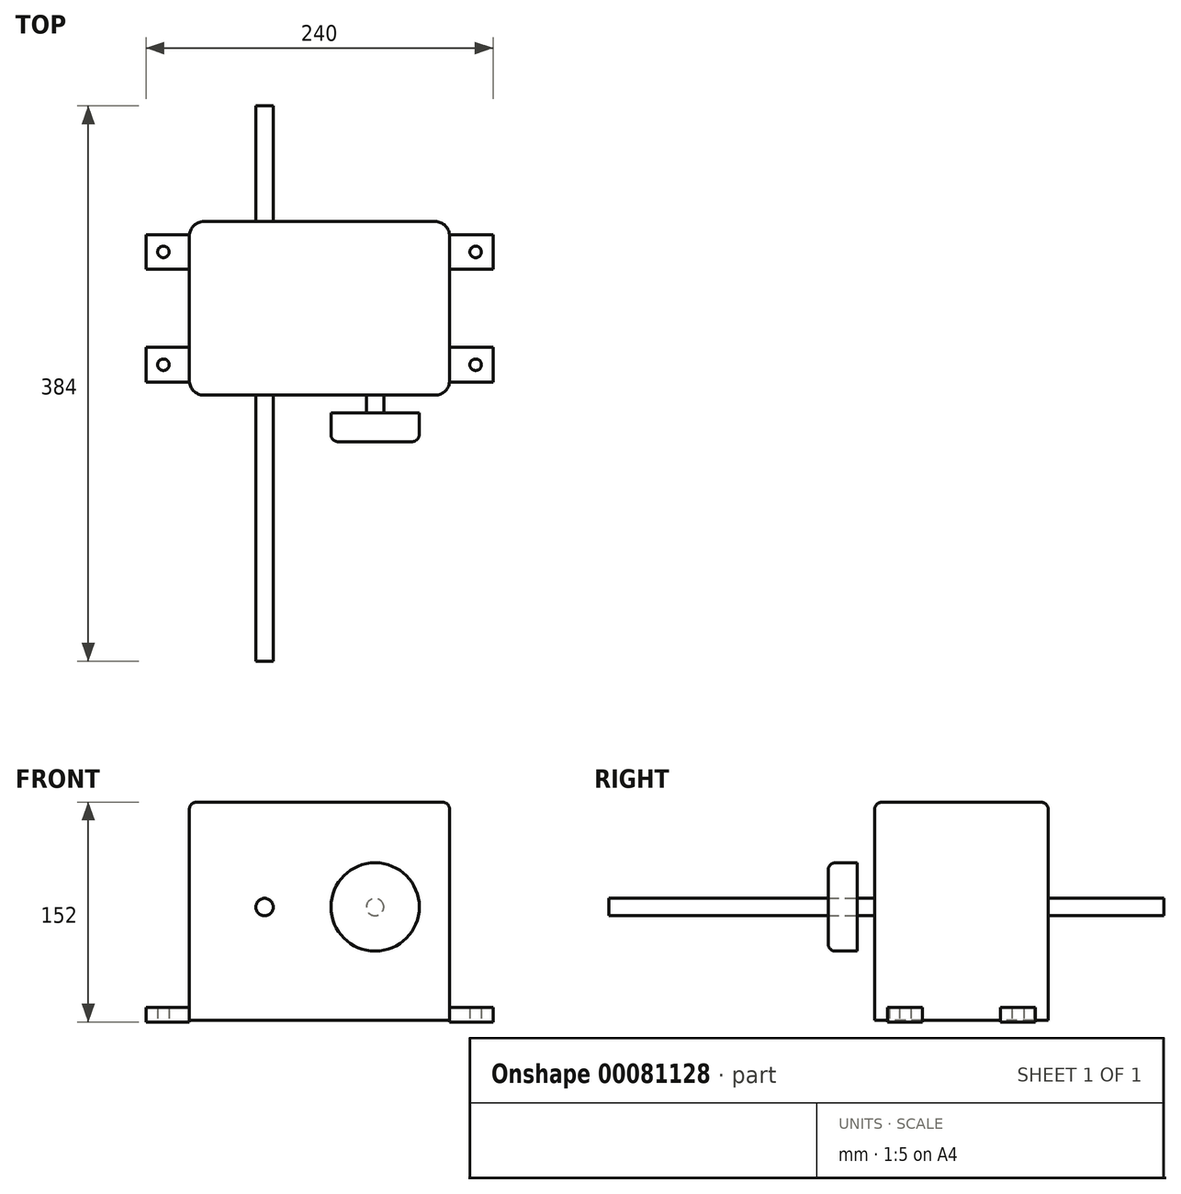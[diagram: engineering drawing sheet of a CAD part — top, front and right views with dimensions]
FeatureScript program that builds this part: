
annotation { "Feature Type Name" : "Feature", "Feature Type Description" : "" }
export const myFeature = defineFeature(function(context is Context, id is Id, definition is map)
    precondition{}
    {
        {
            var Q0;
            Q0=qCreatedBy(makeId("Top.planeOp"),FACE);
            var sketch = newSketch(context, id + "F0", { "sketchPlane" : qUnion([Q0])});
            skLineSegment(sketch, "E0.bottom", {"start": v(-90, 60) * mm, "end": v(90, 60) * mm});
            skLineSegment(sketch, "E0.top", {"start": v(-90, -60) * mm, "end": v(90, -60) * mm});
            skLineSegment(sketch, "E0.left", {"start": v(-90, 60) * mm, "end": v(-90, -60) * mm});
            skLineSegment(sketch, "E0.right", {"start": v(90, 60) * mm, "end": v(90, -60) * mm});
            skLineSegment(sketch, "E1", {"start": v(-90, 60) * mm, "end": v(90, -60) * mm, "construction": true});
            skSolve(sketch);
        }
        {
            var Q0;
            Q0=makeQuery(id+"F0.imprint","IMPRINT",FACE,{"disambiguationData":[TD([[makeQuery(id+"F0.imprint","IMPRINT",EDGE,{"derivedFrom":sQuery(id+"F0.wireOp",EDGE,"E0.bottom")}),-1.0]])]});
            extrude(context, id + "F1", {"entities" : qUnion([Q0]), "depth" : 151 * mm});
        }
        {
            var Q0;
            Q0=makeQuery(id+"F1.opExtrude","SWEPT_EDGE",EDGE,{"disambiguationData":[OSD([sQuery(id+"F0.wireOp",EDGE,"E0.top"),sQuery(id+"F0.wireOp",EDGE,"E0.left")])]});
            var Q1;
            Q1=makeQuery(id+"F1.opExtrude","SWEPT_EDGE",EDGE,{"disambiguationData":[OSD([sQuery(id+"F0.wireOp",EDGE,"E0.top"),sQuery(id+"F0.wireOp",EDGE,"E0.right")])]});
            var Q2;
            Q2=makeQuery(id+"F1.opExtrude","SWEPT_EDGE",EDGE,{"disambiguationData":[OSD([sQuery(id+"F0.wireOp",EDGE,"E0.bottom"),sQuery(id+"F0.wireOp",EDGE,"E0.right")])]});
            var Q3;
            Q3=makeQuery(id+"F1.opExtrude","SWEPT_EDGE",EDGE,{"disambiguationData":[OSD([sQuery(id+"F0.wireOp",EDGE,"E0.bottom"),sQuery(id+"F0.wireOp",EDGE,"E0.left")])]});
            fillet(context, id + "F2", {"entities" : qUnion([Q0, Q1, Q2, Q3]), "radius" : 10 * mm, "tangentPropagation" : true, "allowEdgeOverflow" : false});
        }
        {
            var Q0;
            Q0=makeQuery(id+"F1.opExtrude","CAP_EDGE",EDGE,{"disambiguationData":[OSD([sQuery(id+"F0.wireOp",EDGE,"E0.top")])],"isStart":false});
            fillet(context, id + "F3", {"entities" : qUnion([Q0]), "radius" : 5 * mm, "tangentPropagation" : true, "allowEdgeOverflow" : false});
        }
        {
            var Q0;
            Q0=qCreatedBy(makeId("Top.planeOp"),FACE);
            cPlane(context, id + "F4", {"entities" : qUnion([Q0]), "cplaneType" : CPlaneType.OFFSET, "offset" : 1 * mm, "oppositeDirection" : true, "width" : 150 * mm, "height" : 150 * mm});
        }
        {
            var Q0;
            Q0=qCreatedBy(id+"F4.planeOp",FACE);
            var sketch = newSketch(context, id + "F5", { "sketchPlane" : qUnion([Q0])});
            skLineSegment(sketch, "E2.bottom", {"start": v(90, 51) * mm, "end": v(120, 51) * mm});
            skLineSegment(sketch, "E2.top", {"start": v(90, 27) * mm, "end": v(120, 27) * mm});
            skLineSegment(sketch, "E2.left", {"start": v(90, 51) * mm, "end": v(90, 27) * mm});
            skLineSegment(sketch, "E2.right", {"start": v(120, 51) * mm, "end": v(120, 27) * mm});
            skCircle(sketch, "E3", {"center": v(108, 39) * mm, "radius": 4 * mm});
            skPoint(sketch, "E3.centerSnap0", {"position": v(90, 39) * mm});
            skLineSegment(sketch, "E4", {"start": v(0, 0) * mm, "end": v(-121.89, 0) * mm, "construction": true});
            skLineSegment(sketch, "E5", {"start": v(0, 0) * mm, "end": v(0, -83.82) * mm, "construction": true});
            skLineSegment(sketch, "E6.MirrorCS", {"start": v(90, -27) * mm, "end": v(120, -27) * mm});
            skLineSegment(sketch, "E7.MirrorCS", {"start": v(120, -51) * mm, "end": v(120, -27) * mm});
            skLineSegment(sketch, "E8.MirrorCS", {"start": v(90, -51) * mm, "end": v(120, -51) * mm});
            skLineSegment(sketch, "E9.MirrorCS", {"start": v(90, -51) * mm, "end": v(90, -27) * mm});
            skCircle(sketch, "E10.MirrorC", {"center": v(108, -39) * mm, "radius": 4 * mm});
            skLineSegment(sketch, "E11.MirrorCS", {"start": v(-90, -51) * mm, "end": v(-120, -51) * mm});
            skLineSegment(sketch, "E12.MirrorCS", {"start": v(-120, -51) * mm, "end": v(-120, -27) * mm});
            skLineSegment(sketch, "E13.MirrorCS", {"start": v(-90, -27) * mm, "end": v(-120, -27) * mm});
            skCircle(sketch, "E14.MirrorC", {"center": v(-108, -39) * mm, "radius": 4 * mm});
            skLineSegment(sketch, "E15.MirrorCS", {"start": v(-90, -51) * mm, "end": v(-90, -27) * mm});
            skLineSegment(sketch, "E16.MirrorCS", {"start": v(-90, 27) * mm, "end": v(-120, 27) * mm});
            skLineSegment(sketch, "E17.MirrorCS", {"start": v(-120, 51) * mm, "end": v(-120, 27) * mm});
            skLineSegment(sketch, "E18.MirrorCS", {"start": v(-90, 51) * mm, "end": v(-120, 51) * mm});
            skLineSegment(sketch, "E19.MirrorCS", {"start": v(-90, 51) * mm, "end": v(-90, 27) * mm});
            skCircle(sketch, "E20.MirrorC", {"center": v(-108, 39) * mm, "radius": 4 * mm});
            skSolve(sketch);
        }
        {
            var Q0;
            Q0=makeQuery(id+"F5.imprint","IMPRINT",FACE,{"disambiguationData":[TD([[makeQuery(id+"F5.imprint","IMPRINT",EDGE,{"derivedFrom":sQuery(id+"F5.wireOp",EDGE,"E2.bottom")}),-1.0]])]});
            var Q1;
            Q1=makeQuery(id+"F5.imprint","IMPRINT",FACE,{"disambiguationData":[TD([[makeQuery(id+"F5.imprint","IMPRINT",EDGE,{"derivedFrom":sQuery(id+"F5.wireOp",EDGE,"E6.MirrorCS")}),-1.0]])]});
            var Q2;
            Q2=makeQuery(id+"F5.imprint","IMPRINT",FACE,{"disambiguationData":[TD([[makeQuery(id+"F5.imprint","IMPRINT",EDGE,{"derivedFrom":sQuery(id+"F5.wireOp",EDGE,"E11.MirrorCS")}),-1.0]])]});
            var Q3;
            Q3=makeQuery(id+"F5.imprint","IMPRINT",FACE,{"disambiguationData":[TD([[makeQuery(id+"F5.imprint","IMPRINT",EDGE,{"derivedFrom":sQuery(id+"F5.wireOp",EDGE,"E16.MirrorCS")}),-1.0]])]});
            extrude(context, id + "F6", {"entities" : qUnion([Q0, Q1, Q2, Q3]), "operationType" : NewBodyOperationType.ADD, "depth" : 10 * mm});
        }
        {
            var Q0;
            Q0=makeQuery(id+"F1.opExtrude","SWEPT_FACE",FACE,{"disambiguationData":[OSD([sQuery(id+"F0.wireOp",EDGE,"E0.top")])]});
            var sketch = newSketch(context, id + "F7", { "sketchPlane" : qUnion([Q0])});
            skCircle(sketch, "E21", {"center": v(38.45, 78.5) * mm, "radius": 6 * mm});
            skCircle(sketch, "E22", {"center": v(-38, 78.5) * mm, "radius": 6 * mm});
            skSolve(sketch);
        }
        {
            var Q0;
            Q0=makeQuery(id+"F7.imprint","IMPRINT",FACE,{"disambiguationData":[TD([[makeQuery(id+"F7.imprint","IMPRINT",EDGE,{"derivedFrom":sQuery(id+"F7.wireOp",EDGE,"E21")}),1.0]])]});
            extrude(context, id + "F8", {"entities" : qUnion([Q0]), "operationType" : NewBodyOperationType.ADD, "depth" : 12.2 * mm});
        }
        {
            var Q0;
            Q0=makeQuery(id+"F7.imprint","IMPRINT",FACE,{"disambiguationData":[TD([[makeQuery(id+"F7.imprint","IMPRINT",EDGE,{"derivedFrom":sQuery(id+"F7.wireOp",EDGE,"E22")}),1.0]])]});
            extrude(context, id + "F9", {"entities" : qUnion([Q0]), "operationType" : NewBodyOperationType.ADD, "depth" : 184 * mm, "hasSecondDirection" : true, "secondDirectionOppositeDirection" : true, "secondDirectionDepth" : 200 * mm});
        }
        {
            var Q0;
            Q0=makeQuery(id+"F8.opExtrude","CAP_FACE",FACE,{"disambiguationData":[OSD([sQuery(id+"F7.wireOp",EDGE,"E21")])],"isStart":false});
            var sketch = newSketch(context, id + "F10", { "sketchPlane" : qUnion([Q0])});
            skCircle(sketch, "E23", {"center": v(38.45, 78.5) * mm, "radius": 30.55 * mm});
            skSolve(sketch);
        }
        {
            var Q0;
            Q0=makeQuery(id+"F10.imprint","IMPRINT",FACE,{"disambiguationData":[TD([[makeQuery(id+"F10.imprint","IMPRINT",EDGE,{"derivedFrom":sQuery(id+"F10.wireOp",EDGE,"E23")}),1.0]])]});
            var Q1;
            Q1=makeQuery(id+"F10.imprint","IMPRINT",FACE,{"disambiguationData":[TD([[makeQuery(id+"F10.imprint","IMPRINT",EDGE,{"derivedFrom":makeQuery(id+"F8.opExtrude","CAP_EDGE",EDGE,{"disambiguationData":[OSD([sQuery(id+"F7.wireOp",EDGE,"E21")])],"isStart":false})}),1.0]])]});
            extrude(context, id + "F11", {"entities" : qUnion([Q0, Q1]), "operationType" : NewBodyOperationType.ADD, "depth" : 20 * mm});
        }
        {
            var Q0;
            Q0=makeQuery(id+"F11.opExtrude","CAP_EDGE",EDGE,{"disambiguationData":[OSD([sQuery(id+"F10.wireOp",EDGE,"E23")])],"isStart":false});
            fillet(context, id + "F12", {"entities" : qUnion([Q0]), "radius" : 5 * mm, "tangentPropagation" : true, "allowEdgeOverflow" : false});
        }
    });
